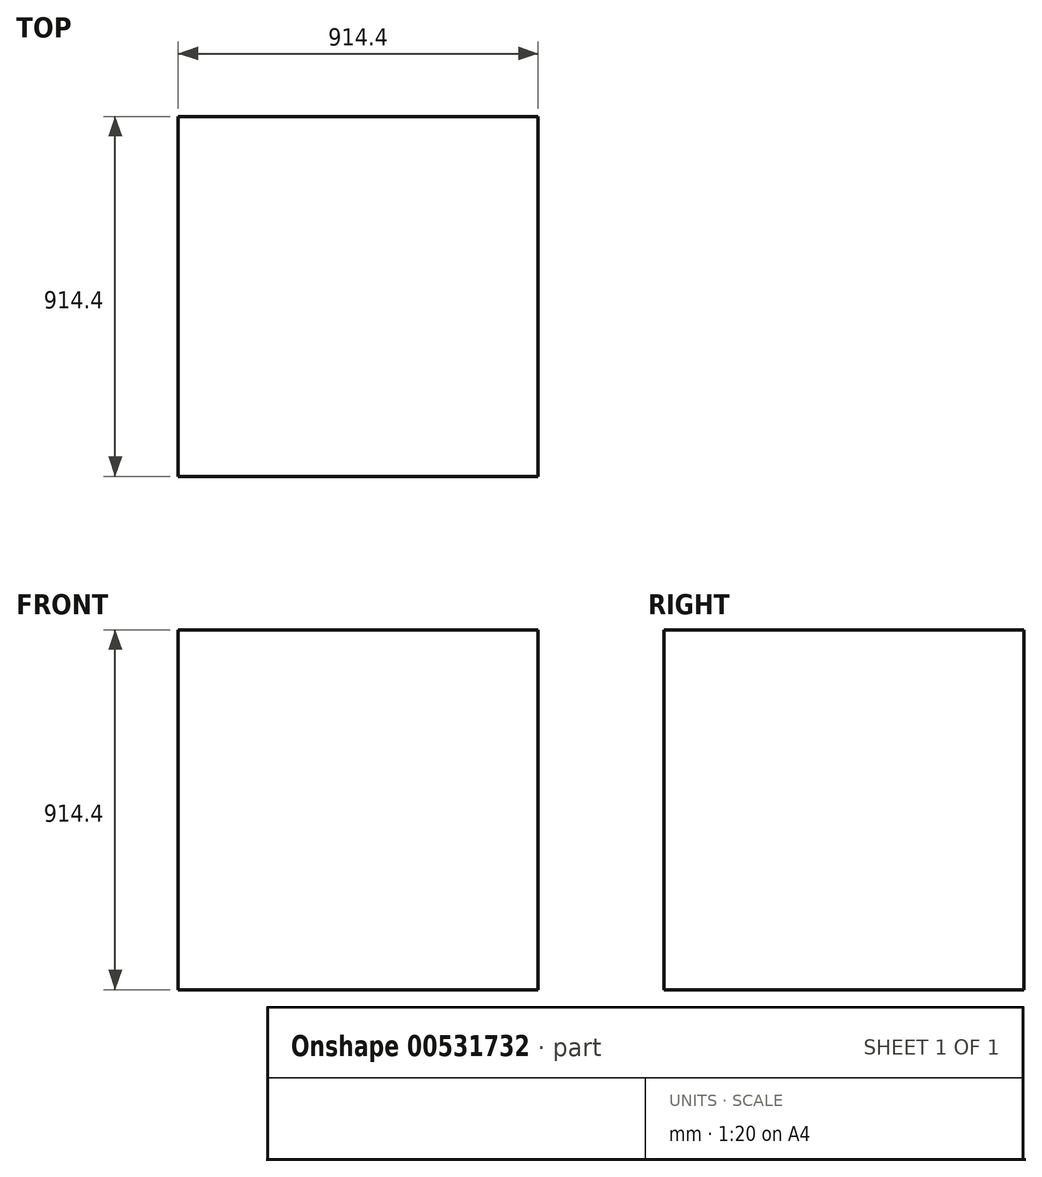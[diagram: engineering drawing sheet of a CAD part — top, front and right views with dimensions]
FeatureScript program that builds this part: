
annotation { "Feature Type Name" : "Feature", "Feature Type Description" : "" }
export const myFeature = defineFeature(function(context is Context, id is Id, definition is map)
    precondition{}
    {
        {
            var Q0;
            Q0=qCreatedBy(makeId("Top.planeOp"),FACE);
            var sketch = newSketch(context, id + "F0", { "sketchPlane" : qUnion([Q0])});
            skLineSegment(sketch, "E0.bottom", {"start": v(-455.35, 481.65) * mm, "end": v(459.05, 481.65) * mm});
            skLineSegment(sketch, "E0.top", {"start": v(-455.35, -432.75) * mm, "end": v(459.05, -432.75) * mm});
            skLineSegment(sketch, "E0.left", {"start": v(-455.35, 481.65) * mm, "end": v(-455.35, -432.75) * mm});
            skLineSegment(sketch, "E0.right", {"start": v(459.05, 481.65) * mm, "end": v(459.05, -432.75) * mm});
            skSolve(sketch);
        }
        {
            var Q0;
            Q0=makeQuery(id+"F0.imprint","IMPRINT",FACE,{"disambiguationData":[TD([[makeQuery(id+"F0.imprint","IMPRINT",EDGE,{"derivedFrom":sQuery(id+"F0.wireOp",EDGE,"E0.bottom")}),-1.0]])]});
            extrude(context, id + "F1", {"entities" : qUnion([Q0]), "depth" : 914.4 * mm, "offsetDistance" : 25.4 * mm});
        }
    });
